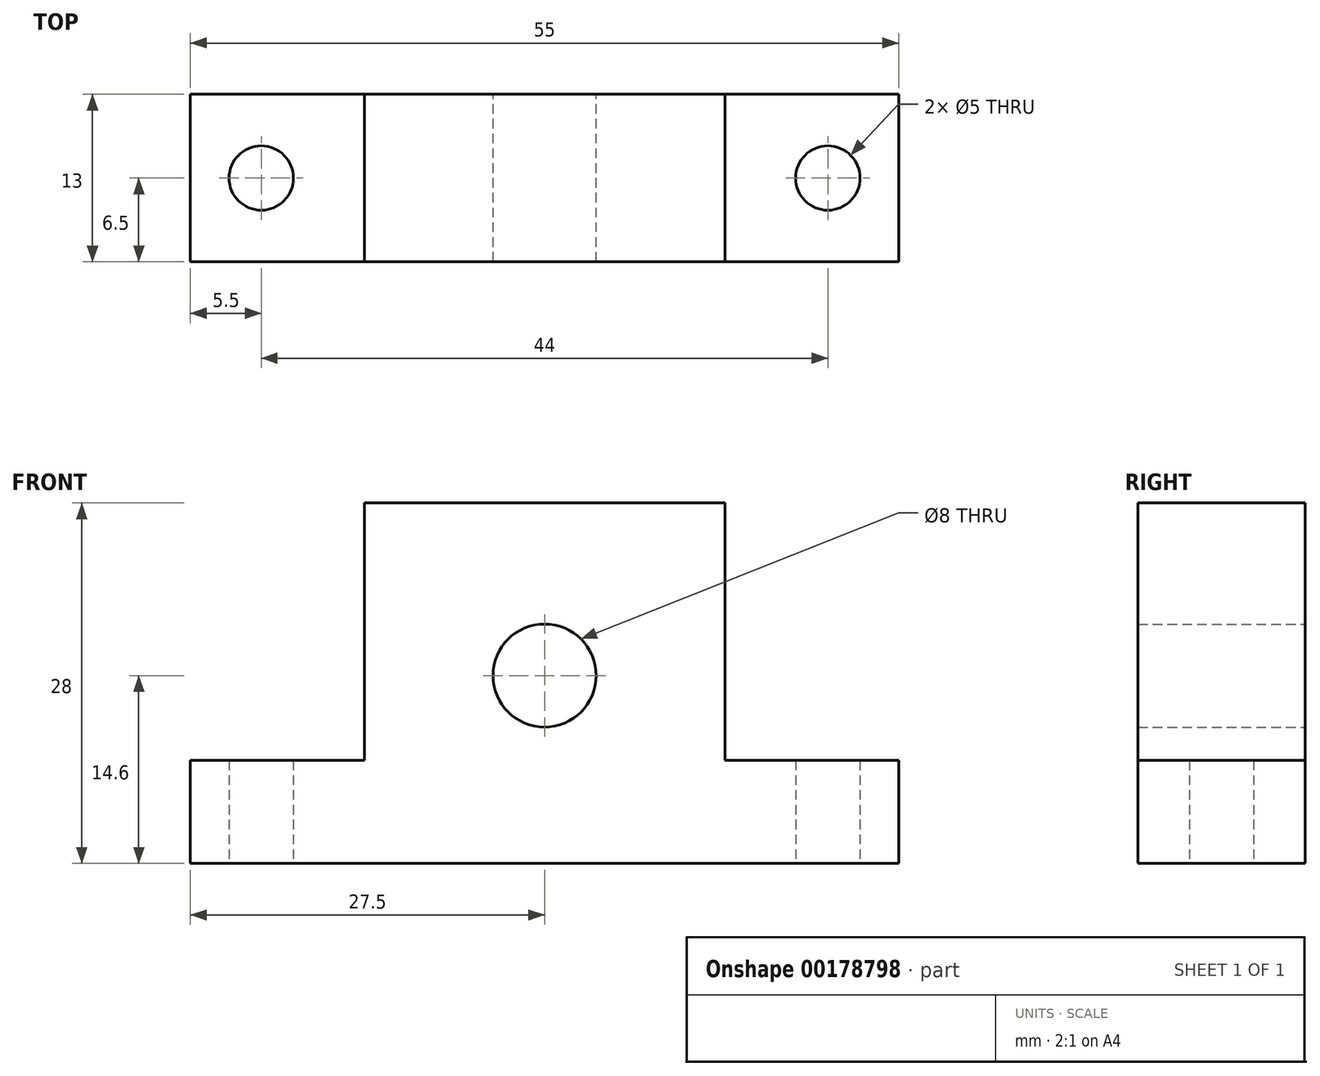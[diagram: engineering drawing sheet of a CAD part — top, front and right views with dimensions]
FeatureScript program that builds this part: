
annotation { "Feature Type Name" : "Feature", "Feature Type Description" : "" }
export const myFeature = defineFeature(function(context is Context, id is Id, definition is map)
    precondition{}
    {
        {
            var Q0;
            Q0=qCreatedBy(makeId("Front.planeOp"),FACE);
            var sketch = newSketch(context, id + "F0", { "sketchPlane" : qUnion([Q0])});
            skLineSegment(sketch, "E0", {"start": v(0, 0) * mm, "end": v(27.5, 0) * mm});
            skLineSegment(sketch, "E1", {"start": v(27.5, 0) * mm, "end": v(27.5, 8) * mm});
            skLineSegment(sketch, "E2", {"start": v(27.5, 8) * mm, "end": v(14, 8) * mm});
            skLineSegment(sketch, "E3", {"start": v(14, 8) * mm, "end": v(14, 28) * mm});
            skLineSegment(sketch, "E4", {"start": v(14, 28) * mm, "end": v(0, 28) * mm});
            skLineSegment(sketch, "E5.MirrorCS", {"start": v(-14, 28) * mm, "end": v(0, 28) * mm});
            skLineSegment(sketch, "E6.MirrorCS", {"start": v(-14, 8) * mm, "end": v(-14, 28) * mm});
            skLineSegment(sketch, "E7.MirrorCS", {"start": v(-27.5, 8) * mm, "end": v(-14, 8) * mm});
            skLineSegment(sketch, "E8.MirrorCS", {"start": v(0, 0) * mm, "end": v(-27.5, 0) * mm});
            skLineSegment(sketch, "E9.MirrorCS", {"start": v(-27.5, 0) * mm, "end": v(-27.5, 8) * mm});
            skCircle(sketch, "E10", {"center": v(0, 14.6) * mm, "radius": 4 * mm});
            skCircle(sketch, "E11", {"center": v(0, 14.6) * mm, "radius": 10.5 * mm});
            skSolve(sketch);
        }
        {
            var Q0;
            Q0=makeQuery(id+"F0.imprint","IMPRINT",FACE,{"disambiguationData":[TD([[makeQuery(id+"F0.imprint","IMPRINT",EDGE,{"derivedFrom":sQuery(id+"F0.wireOp",EDGE,"E0")}),1.0]])]});
            var Q1;
            Q1=makeQuery(id+"F0.imprint","IMPRINT",FACE,{"disambiguationData":[TD([[makeQuery(id+"F0.imprint","IMPRINT",EDGE,{"derivedFrom":sQuery(id+"F0.wireOp",EDGE,"E10")}),-1.0]])]});
            extrude(context, id + "F1", {"entities" : qUnion([Q0, Q1]), "endBound" : BoundingType.SYMMETRIC, "depth" : 13 * mm});
        }
        {
            var Q0;
            Q0=qCreatedBy(makeId("Top.planeOp"),FACE);
            var sketch = newSketch(context, id + "F2", { "sketchPlane" : qUnion([Q0])});
            skCircle(sketch, "E12", {"center": v(22, 0) * mm, "radius": 2.5 * mm});
            skLineSegment(sketch, "E13", {"start": v(0, 0) * mm, "end": v(27.45, 0) * mm, "construction": true});
            skCircle(sketch, "E14.MirrorC", {"center": v(-22, 0) * mm, "radius": 2.5 * mm});
            skSolve(sketch);
        }
        {
            var Q0;
            Q0 = qSketchRegion(id + "F2", true);
            extrude(context, id + "F3", {"entities" : qUnion([Q0]), "operationType" : NewBodyOperationType.REMOVE, "endBound" : BoundingType.UP_TO_NEXT, "depth" : 25 * mm});
        }
    });
